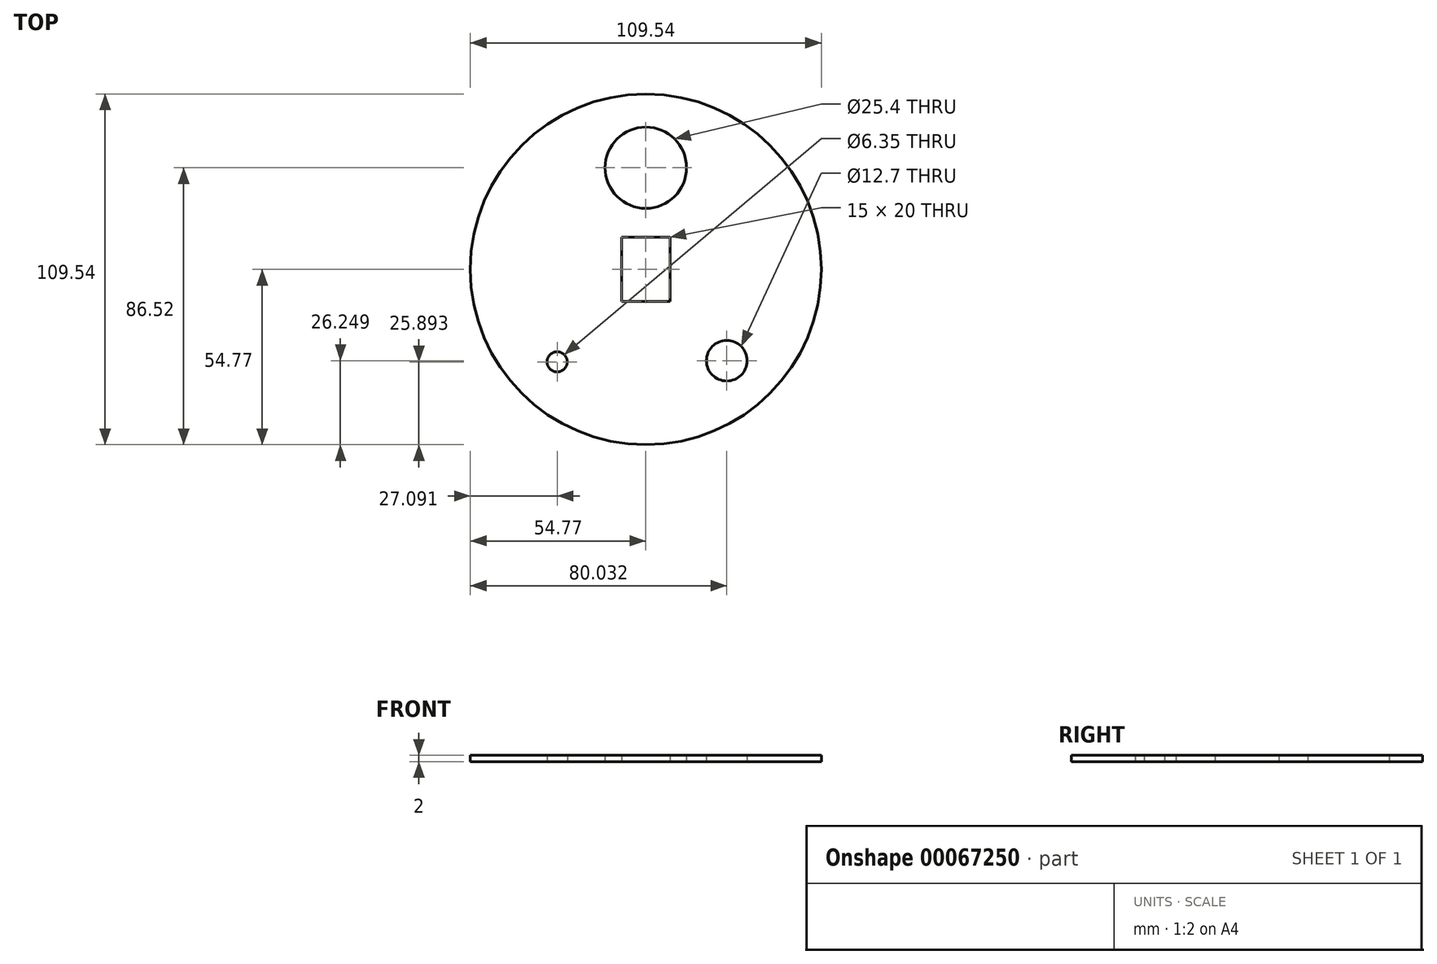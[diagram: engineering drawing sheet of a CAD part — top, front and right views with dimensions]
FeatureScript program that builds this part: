
annotation { "Feature Type Name" : "Feature", "Feature Type Description" : "" }
export const myFeature = defineFeature(function(context is Context, id is Id, definition is map)
    precondition{}
    {
        {
            var Q0;
            Q0=qCreatedBy(makeId("Top.planeOp"),FACE);
            var sketch = newSketch(context, id + "F0", { "sketchPlane" : qUnion([Q0])});
            skCircle(sketch, "E0", {"center": v(0, 0) * mm, "radius": 54.77 * mm});
            skLineSegment(sketch, "E1.bottom", {"start": v(-7.5, 10) * mm, "end": v(7.5, 10) * mm});
            skLineSegment(sketch, "E1.top", {"start": v(-7.5, -10) * mm, "end": v(7.5, -10) * mm});
            skLineSegment(sketch, "E1.left", {"start": v(-7.5, 10) * mm, "end": v(-7.5, -10) * mm});
            skLineSegment(sketch, "E1.right", {"start": v(7.5, 10) * mm, "end": v(7.5, -10) * mm});
            skCircle(sketch, "E2", {"center": v(0, 31.75) * mm, "radius": 12.7 * mm});
            skCircle(sketch, "E3", {"center": v(-27.68, -28.88) * mm, "radius": 3.18 * mm});
            skCircle(sketch, "E4", {"center": v(25.26, -28.52) * mm, "radius": 6.35 * mm});
            skSolve(sketch);
        }
        {
            var Q0;
            Q0=qSketchRegion(id+"F0",true);
            extrude(context, id + "F1", {"entities" : qUnion([Q0]), "depth" : 2 * mm});
        }
    });
